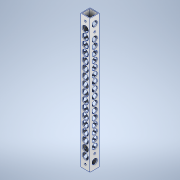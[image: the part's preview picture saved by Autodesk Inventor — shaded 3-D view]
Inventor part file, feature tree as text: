
AUTODESK INVENTOR PART (.ipt)
format: ipt  version: 2020.3 (Build 243373000, 373)  size: 239,616 bytes
history: native  units: mm
features: sketch x5, hole x4, other x1, extrude x1
ambient origin geometry x8: Origin, YZ Plane, XZ Plane, XY Plane, X Axis, Y Axis, Z Axis, Center Point
bodies: Body1 (feature_tree)
feature tree (11):
  other  "ソリッド1"
  extrude  "押し出し1"  Depth=15.0mm
  hole  "穴1"  [1 undecoded]
  hole  "穴2"  [1 undecoded]
  hole  "穴3"  [1 undecoded]
  hole  "穴4"  [1 undecoded]
  sketch  "スケッチ1"
  sketch  "スケッチ2"
  sketch  "スケッチ3"
  sketch  "スケッチ4"
  sketch  "スケッチ5"
note: 4 required parameter values undecoded (feature->parameter linkage not recoverable at this tier; creation-order binding heuristic only, values carry confidence <= 0.55)
